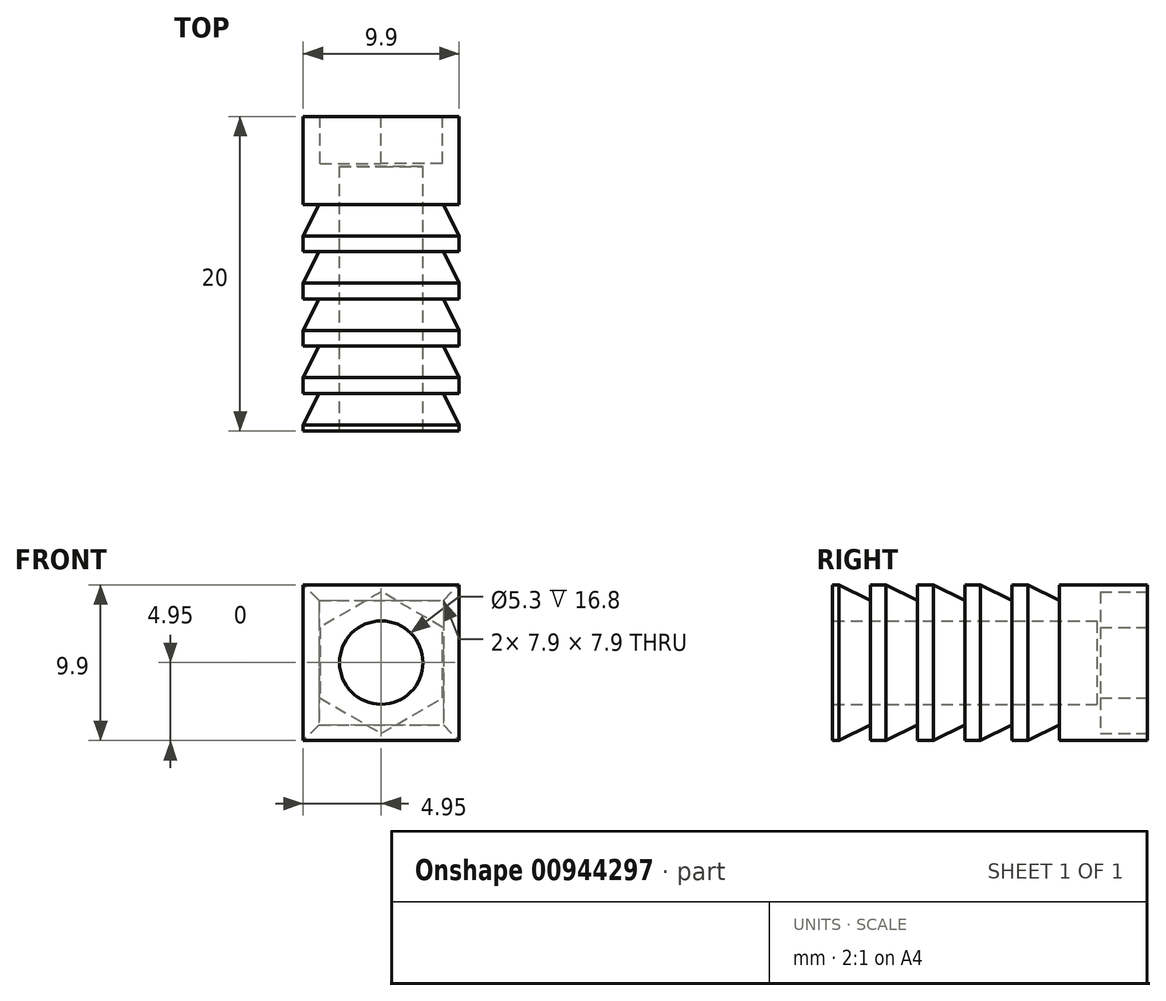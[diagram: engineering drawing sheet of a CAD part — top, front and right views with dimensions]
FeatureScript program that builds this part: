
annotation { "Feature Type Name" : "Feature", "Feature Type Description" : "" }
export const myFeature = defineFeature(function(context is Context, id is Id, definition is map)
    precondition{}
    {
        {
            var Q0;
            Q0=qCreatedBy(makeId("Front.planeOp"),FACE);
            var sketch = newSketch(context, id + "F0", { "sketchPlane" : qUnion([Q0])});
            skLineSegment(sketch, "E0.bottom", {"start": v(4.95, -4.95) * mm, "end": v(-4.95, -4.95) * mm});
            skLineSegment(sketch, "E0.top", {"start": v(4.95, 4.95) * mm, "end": v(-4.95, 4.95) * mm});
            skLineSegment(sketch, "E0.left", {"start": v(4.95, -4.95) * mm, "end": v(4.95, 4.95) * mm});
            skLineSegment(sketch, "E0.right", {"start": v(-4.95, -4.95) * mm, "end": v(-4.95, 4.95) * mm});
            skPoint(sketch, "E0.middle", {"position": v(0, 0) * mm});
            skSolve(sketch);
        }
        {
            var Q0;
            Q0 = qSketchRegion(id + "F0", true);
            extrude(context, id + "F1", {"entities" : qUnion([Q0]), "depth" : 20 * mm, "offsetDistance" : 25 * mm});
        }
        {
            var Q0;
            Q0=makeQuery(id+"F1.opExtrude","SWEPT_FACE",FACE,{"disambiguationData":[OSD([sQuery(id+"F0.wireOp",EDGE,"E0.bottom")])]});
            var sketch = newSketch(context, id + "F2", { "sketchPlane" : qUnion([Q0])});
            skLineSegment(sketch, "E1", {"start": v(4.95, 7.6) * mm, "end": v(4.95, 5.6) * mm});
            skLineSegment(sketch, "E2", {"start": v(0, 0) * mm, "end": v(0, 20) * mm, "construction": true});
            skLineSegment(sketch, "E3.direction1", {"start": v(4.95, 5.6) * mm, "end": v(4.95, 8.6) * mm, "construction": true});
            skLineSegment(sketch, "E4", {"start": v(4.95, 5.6) * mm, "end": v(3.95, 5.6) * mm});
            skLineSegment(sketch, "E5", {"start": v(3.95, 5.6) * mm, "end": v(4.95, 7.6) * mm});
            skLineSegment(sketch, "E6.1.0.0", {"start": v(3.95, 8.6) * mm, "end": v(4.95, 10.6) * mm});
            skLineSegment(sketch, "E6.1.0.1", {"start": v(4.95, 8.6) * mm, "end": v(3.95, 8.6) * mm});
            skLineSegment(sketch, "E6.1.0.2", {"start": v(4.95, 8.6) * mm, "end": v(4.95, 11.6) * mm, "construction": true});
            skLineSegment(sketch, "E6.2.0.0", {"start": v(3.95, 11.6) * mm, "end": v(4.95, 13.6) * mm});
            skLineSegment(sketch, "E6.2.0.1", {"start": v(4.95, 11.6) * mm, "end": v(3.95, 11.6) * mm});
            skLineSegment(sketch, "E6.2.0.2", {"start": v(4.95, 11.6) * mm, "end": v(4.95, 14.6) * mm, "construction": true});
            skLineSegment(sketch, "E6.3.0.0", {"start": v(3.95, 14.6) * mm, "end": v(4.95, 16.6) * mm});
            skLineSegment(sketch, "E6.3.0.1", {"start": v(4.95, 14.6) * mm, "end": v(3.95, 14.6) * mm});
            skLineSegment(sketch, "E6.3.0.2", {"start": v(4.95, 14.6) * mm, "end": v(4.95, 17.6) * mm, "construction": true});
            skLineSegment(sketch, "E6.direction1", {"start": v(3.95, 5.6) * mm, "end": v(3.95, 8.6) * mm, "construction": true});
            skLineSegment(sketch, "E7.MirrorCS", {"start": v(-4.95, 7.6) * mm, "end": v(-4.95, 5.6) * mm});
            skLineSegment(sketch, "E8.MirrorCS", {"start": v(-3.95, 8.6) * mm, "end": v(-4.95, 10.6) * mm});
            skLineSegment(sketch, "E9.MirrorCS", {"start": v(-4.95, 11.6) * mm, "end": v(-3.95, 11.6) * mm});
            skLineSegment(sketch, "E10.MirrorCS", {"start": v(-3.95, 5.6) * mm, "end": v(-4.95, 7.6) * mm});
            skLineSegment(sketch, "E11.MirrorCS", {"start": v(-4.95, 14.6) * mm, "end": v(-3.95, 14.6) * mm});
            skLineSegment(sketch, "E12.MirrorCS", {"start": v(-3.95, 11.6) * mm, "end": v(-4.95, 13.6) * mm});
            skLineSegment(sketch, "E13.MirrorCS", {"start": v(-4.95, 8.6) * mm, "end": v(-4.95, 11.6) * mm, "construction": true});
            skLineSegment(sketch, "E14.MirrorCS", {"start": v(-3.95, 14.6) * mm, "end": v(-4.95, 16.6) * mm});
            skLineSegment(sketch, "E15.MirrorCS", {"start": v(-4.95, 11.6) * mm, "end": v(-4.95, 14.6) * mm, "construction": true});
            skLineSegment(sketch, "E16.MirrorCS", {"start": v(-3.95, 5.6) * mm, "end": v(-3.95, 8.6) * mm, "construction": true});
            skLineSegment(sketch, "E17.MirrorCS", {"start": v(-4.95, 8.6) * mm, "end": v(-3.95, 8.6) * mm});
            skLineSegment(sketch, "E18.MirrorCS", {"start": v(-4.95, 5.6) * mm, "end": v(-4.95, 8.6) * mm, "construction": true});
            skLineSegment(sketch, "E19.MirrorCS", {"start": v(-4.95, 5.6) * mm, "end": v(-3.95, 5.6) * mm});
            skLineSegment(sketch, "E20.0.4.0", {"start": v(3.95, 17.6) * mm, "end": v(4.95, 19.6) * mm});
            skLineSegment(sketch, "E20.3.4.0", {"start": v(4.95, 17.6) * mm, "end": v(3.95, 17.6) * mm});
            skLineSegment(sketch, "E20.6.4.0", {"start": v(4.95, 17.6) * mm, "end": v(4.95, 20.6) * mm, "construction": true});
            skLineSegment(sketch, "E21.MirrorCS", {"start": v(-4.95, 17.6) * mm, "end": v(-3.95, 17.6) * mm});
            skLineSegment(sketch, "E22.MirrorCS", {"start": v(-3.95, 17.6) * mm, "end": v(-4.95, 19.6) * mm});
            skSolve(sketch);
        }
        {
            var Q0;
            Q0=makeQuery(id+"F2.imprint","IMPRINT",FACE,{"disambiguationData":[TD([[makeQuery(id+"F2.imprint","IMPRINT",EDGE,{"derivedFrom":sQuery(id+"F2.wireOp",EDGE,"E7.MirrorCS")}),1.0]])]});
            var Q1;
            {var subQ0=sQuery(id+"F2.wireOp",EDGE,"E8.MirrorCS");Q1=makeQuery(id+"F2.imprint","IMPRINT",FACE,{"disambiguationData":[TD([[makeQuery(id+"F2.imprint","IMPRINT",EDGE,{"derivedFrom":subQ0}),1.0]])]});}
            var Q2;
            {var subQ0=sQuery(id+"F2.wireOp",EDGE,"E9.MirrorCS");Q2=makeQuery(id+"F2.imprint","IMPRINT",FACE,{"disambiguationData":[TD([[makeQuery(id+"F2.imprint","IMPRINT",EDGE,{"derivedFrom":subQ0}),1.0]])]});}
            var Q3;
            {var subQ0=sQuery(id+"F2.wireOp",EDGE,"E11.MirrorCS");Q3=makeQuery(id+"F2.imprint","IMPRINT",FACE,{"disambiguationData":[TD([[makeQuery(id+"F2.imprint","IMPRINT",EDGE,{"derivedFrom":subQ0}),1.0]])]});}
            var Q4;
            {var subQ0=sQuery(id+"F2.wireOp",EDGE,"E21.MirrorCS");Q4=makeQuery(id+"F2.imprint","IMPRINT",FACE,{"disambiguationData":[TD([[makeQuery(id+"F2.imprint","IMPRINT",EDGE,{"derivedFrom":subQ0}),1.0]])]});}
            var Q5;
            Q5=makeQuery(id+"F2.imprint","IMPRINT",FACE,{"disambiguationData":[TD([[makeQuery(id+"F2.imprint","IMPRINT",EDGE,{"derivedFrom":sQuery(id+"F2.wireOp",EDGE,"E1")}),-1.0]])]});
            var Q6;
            {var subQ0=sQuery(id+"F2.wireOp",EDGE,"E6.1.0.0");Q6=makeQuery(id+"F2.imprint","IMPRINT",FACE,{"disambiguationData":[TD([[makeQuery(id+"F2.imprint","IMPRINT",EDGE,{"derivedFrom":subQ0}),-1.0]])]});}
            var Q7;
            {var subQ0=sQuery(id+"F2.wireOp",EDGE,"E6.2.0.0");Q7=makeQuery(id+"F2.imprint","IMPRINT",FACE,{"disambiguationData":[TD([[makeQuery(id+"F2.imprint","IMPRINT",EDGE,{"derivedFrom":subQ0}),-1.0]])]});}
            var Q8;
            {var subQ0=sQuery(id+"F2.wireOp",EDGE,"E6.3.0.0");Q8=makeQuery(id+"F2.imprint","IMPRINT",FACE,{"disambiguationData":[TD([[makeQuery(id+"F2.imprint","IMPRINT",EDGE,{"derivedFrom":subQ0}),-1.0]])]});}
            var Q9;
            {var subQ0=sQuery(id+"F2.wireOp",EDGE,"E20.0.4.0");Q9=makeQuery(id+"F2.imprint","IMPRINT",FACE,{"disambiguationData":[TD([[makeQuery(id+"F2.imprint","IMPRINT",EDGE,{"derivedFrom":subQ0}),-1.0]])]});}
            extrude(context, id + "F3", {"entities" : qUnion([Q0, Q1, Q2, Q3, Q4, Q5, Q6, Q7, Q8, Q9]), "operationType" : NewBodyOperationType.REMOVE, "endBound" : BoundingType.THROUGH_ALL, "oppositeDirection" : true, "depth" : 25 * mm, "offsetDistance" : 25 * mm});
        }
        {
            var Q0;
            Q0=makeQuery(id+"F1.opExtrude","SWEPT_FACE",FACE,{"disambiguationData":[OSD([sQuery(id+"F0.wireOp",EDGE,"E0.left")])]});
            var sketch = newSketch(context, id + "F4", { "sketchPlane" : qUnion([Q0])});
            skLineSegment(sketch, "E23", {"start": v(-23.22, 0) * mm, "end": v(-3.22, 0) * mm, "construction": true});
            skLineSegment(sketch, "E24", {"start": v(-20, 0) * mm, "end": v(0, 0) * mm, "construction": true});
            skLineSegment(sketch, "E25", {"start": v(10.12, 2.51) * mm, "end": v(10.12, 0.51) * mm});
            skLineSegment(sketch, "E26.direction1", {"start": v(10.12, 0.51) * mm, "end": v(10.12, 4.51) * mm, "construction": true});
            skLineSegment(sketch, "E27", {"start": v(10.12, 0.51) * mm, "end": v(9.12, 0.51) * mm});
            skLineSegment(sketch, "E28", {"start": v(9.12, 0.51) * mm, "end": v(10.12, 2.51) * mm});
            skLineSegment(sketch, "E29.direction1", {"start": v(9.12, 0.51) * mm, "end": v(9.12, 4.51) * mm, "construction": true});
            skLineSegment(sketch, "E30", {"start": v(-5.6, 4.95) * mm, "end": v(-7.6, 4.95) * mm});
            skLineSegment(sketch, "E31", {"start": v(-7.6, 4.95) * mm, "end": v(-5.6, 4.95) * mm});
            skLineSegment(sketch, "E32", {"start": v(-5.6, 4.95) * mm, "end": v(-5.6, 3.95) * mm});
            skLineSegment(sketch, "E33", {"start": v(-5.6, 3.95) * mm, "end": v(-7.6, 4.95) * mm});
            skLineSegment(sketch, "E34.1.0.0", {"start": v(-10.6, 4.95) * mm, "end": v(-8.6, 4.95) * mm});
            skLineSegment(sketch, "E34.1.0.1", {"start": v(-8.6, 3.95) * mm, "end": v(-10.6, 4.95) * mm});
            skLineSegment(sketch, "E34.1.0.2", {"start": v(-8.6, 4.95) * mm, "end": v(-8.6, 3.95) * mm});
            skLineSegment(sketch, "E34.2.0.0", {"start": v(-13.6, 4.95) * mm, "end": v(-11.6, 4.95) * mm});
            skLineSegment(sketch, "E34.2.0.1", {"start": v(-11.6, 3.95) * mm, "end": v(-13.6, 4.95) * mm});
            skLineSegment(sketch, "E34.2.0.2", {"start": v(-11.6, 4.95) * mm, "end": v(-11.6, 3.95) * mm});
            skLineSegment(sketch, "E34.direction1", {"start": v(-7.6, 4.95) * mm, "end": v(-10.6, 4.95) * mm, "construction": true});
            skLineSegment(sketch, "E35.0.3.0", {"start": v(-16.6, 4.95) * mm, "end": v(-14.6, 4.95) * mm});
            skLineSegment(sketch, "E35.3.3.0", {"start": v(-14.6, 3.95) * mm, "end": v(-16.6, 4.95) * mm});
            skLineSegment(sketch, "E35.6.3.0", {"start": v(-14.6, 4.95) * mm, "end": v(-14.6, 3.95) * mm});
            skLineSegment(sketch, "E36.MirrorCS", {"start": v(-8.6, -4.95) * mm, "end": v(-8.6, -3.95) * mm});
            skLineSegment(sketch, "E37.MirrorCS", {"start": v(-14.6, -4.95) * mm, "end": v(-14.6, -3.95) * mm});
            skLineSegment(sketch, "E38.MirrorCS", {"start": v(-5.6, -4.95) * mm, "end": v(-5.6, -3.95) * mm});
            skLineSegment(sketch, "E39.MirrorCS", {"start": v(-11.6, -4.95) * mm, "end": v(-11.6, -3.95) * mm});
            skLineSegment(sketch, "E40.MirrorCS", {"start": v(-5.6, -4.95) * mm, "end": v(-7.6, -4.95) * mm});
            skLineSegment(sketch, "E41.MirrorCS", {"start": v(-10.6, -4.95) * mm, "end": v(-8.6, -4.95) * mm});
            skLineSegment(sketch, "E42.MirrorCS", {"start": v(-13.6, -4.95) * mm, "end": v(-11.6, -4.95) * mm});
            skLineSegment(sketch, "E43.MirrorCS", {"start": v(-11.6, -3.95) * mm, "end": v(-13.6, -4.95) * mm});
            skLineSegment(sketch, "E44.MirrorCS", {"start": v(-7.6, -4.95) * mm, "end": v(-10.6, -4.95) * mm, "construction": true});
            skLineSegment(sketch, "E45.MirrorCS", {"start": v(-7.6, -4.95) * mm, "end": v(-5.6, -4.95) * mm});
            skLineSegment(sketch, "E46.MirrorCS", {"start": v(-16.6, -4.95) * mm, "end": v(-14.6, -4.95) * mm});
            skLineSegment(sketch, "E47.MirrorCS", {"start": v(-8.6, -3.95) * mm, "end": v(-10.6, -4.95) * mm});
            skLineSegment(sketch, "E48.MirrorCS", {"start": v(-5.6, -3.95) * mm, "end": v(-7.6, -4.95) * mm});
            skLineSegment(sketch, "E49.MirrorCS", {"start": v(-14.6, -3.95) * mm, "end": v(-16.6, -4.95) * mm});
            skLineSegment(sketch, "E50.0.4.0", {"start": v(-19.6, 4.95) * mm, "end": v(-17.6, 4.95) * mm});
            skLineSegment(sketch, "E50.3.4.0", {"start": v(-17.6, 3.95) * mm, "end": v(-19.6, 4.95) * mm});
            skLineSegment(sketch, "E50.6.4.0", {"start": v(-17.6, 4.95) * mm, "end": v(-17.6, 3.95) * mm});
            skLineSegment(sketch, "E51.MirrorCS", {"start": v(-17.6, -3.95) * mm, "end": v(-19.6, -4.95) * mm});
            skLineSegment(sketch, "E52.MirrorCS", {"start": v(-17.6, -4.95) * mm, "end": v(-17.6, -3.95) * mm});
            skLineSegment(sketch, "E53.MirrorCS", {"start": v(-19.6, -4.95) * mm, "end": v(-17.6, -4.95) * mm});
            skSolve(sketch);
        }
        {
            var Q0;
            Q0 = qSketchRegion(id + "F4", true);
            extrude(context, id + "F5", {"entities" : qUnion([Q0]), "operationType" : NewBodyOperationType.REMOVE, "endBound" : BoundingType.THROUGH_ALL, "oppositeDirection" : true, "depth" : 25 * mm, "offsetDistance" : 25 * mm});
        }
        {
            var Q0;
            Q0=makeQuery(id+"F1.opExtrude","CAP_FACE",FACE,{"disambiguationData":[OSD([sQuery(id+"F0.wireOp",EDGE,"E0.bottom"),sQuery(id+"F0.wireOp",EDGE,"E0.top"),sQuery(id+"F0.wireOp",EDGE,"E0.left"),sQuery(id+"F0.wireOp",EDGE,"E0.right")])],"isStart":true});
            var sketch = newSketch(context, id + "F6", { "sketchPlane" : qUnion([Q0])});
            skCircle(sketch, "E54", {"center": v(0, 0) * mm, "radius": 2.65 * mm});
            skSolve(sketch);
        }
        {
            var Q0;
            Q0=makeQuery(id+"F6.imprint","IMPRINT",FACE,{"disambiguationData":[TD([[makeQuery(id+"F6.imprint","IMPRINT",EDGE,{"derivedFrom":sQuery(id+"F6.wireOp",EDGE,"E54")}),1.0]])]});
            extrude(context, id + "F7", {"entities" : qUnion([Q0]), "operationType" : NewBodyOperationType.REMOVE, "endBound" : BoundingType.THROUGH_ALL, "oppositeDirection" : true, "depth" : 25 * mm, "offsetDistance" : 25 * mm});
        }
        {
            var Q0;
            Q0=makeQuery(id+"F1.opExtrude","CAP_FACE",FACE,{"disambiguationData":[OSD([sQuery(id+"F0.wireOp",EDGE,"E0.bottom"),sQuery(id+"F0.wireOp",EDGE,"E0.top"),sQuery(id+"F0.wireOp",EDGE,"E0.left"),sQuery(id+"F0.wireOp",EDGE,"E0.right")])],"isStart":true});
            var sketch = newSketch(context, id + "F8", { "sketchPlane" : qUnion([Q0])});
            skCircle(sketch, "E55.cCircle", {"center": v(0, 0) * mm, "radius": 4.5 * mm, "construction": true});
            skLineSegment(sketch, "E55.0", {"start": v(3.9, -2.25) * mm, "end": v(0, -4.5) * mm});
            skLineSegment(sketch, "E55.1", {"start": v(0, -4.5) * mm, "end": v(-3.9, -2.25) * mm});
            skLineSegment(sketch, "E55.2", {"start": v(-3.9, -2.25) * mm, "end": v(-3.9, 2.25) * mm});
            skLineSegment(sketch, "E55.3", {"start": v(-3.9, 2.25) * mm, "end": v(0, 4.5) * mm});
            skLineSegment(sketch, "E55.4", {"start": v(0, 4.5) * mm, "end": v(3.9, 2.25) * mm});
            skLineSegment(sketch, "E55.5", {"start": v(3.9, 2.25) * mm, "end": v(3.9, -2.25) * mm});
            skSolve(sketch);
        }
        {
            var Q0;
            Q0 = qSketchRegion(id + "F8", true);
            extrude(context, id + "F9", {"entities" : qUnion([Q0]), "operationType" : NewBodyOperationType.REMOVE, "oppositeDirection" : true, "depth" : 3 * mm, "offsetDistance" : 25 * mm});
        }
        {
            var Q0;
            Q0 = qSketchRegion(id + "F8", true);
            extrude(context, id + "F10", {"entities" : qUnion([Q0]), "operationType" : NewBodyOperationType.ADD, "oppositeDirection" : true, "depth" : 3.2 * mm, "offsetDistance" : 25 * mm, "hasSecondDirection" : true, "secondDirectionOppositeDirection" : true, "secondDirectionDepth" : 3 * mm});
        }
    });
